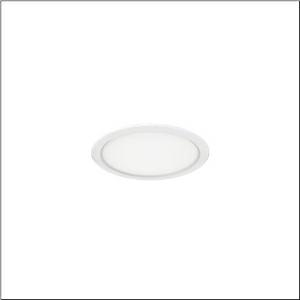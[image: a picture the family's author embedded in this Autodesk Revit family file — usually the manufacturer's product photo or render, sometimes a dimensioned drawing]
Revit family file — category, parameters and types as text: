
# Revit family: lunis_41_eco_51ds107d43b
name_source: partatom
category: Lighting Fixtures
units: mm (PartAtom-declared; Revit-internal decimal feet)

## family parameters
Cut with Voids When Loaded = No
Host = Face
Light Source = No
Part Type = Normal
Room Calculation Point = No
Round Connector Dimension = Use Diameter
Shared = No

## types (1)
- Lunis 41 Eco (1 x LED, 1580 lm, 12 W, 4000K)
    Apparent Load = 12 VA
    CIE Flux Codes = 47 80 97 100 100
    Color Rendering = 80
    Color Temperature = 4000K
    Default Elevation = 1800 mm
    Description = Lunis 41,  Eco, downlight, light emission: direct distribution, LED rated luminous flux: 1.580lm, light colour: 840, mains connection: 230V, AC, 50/60Hz, housing, round, of aluminium, coated, traffic white (RAL 9016), diameter: 166mm, recess depth: 54mm, protection rating (complete): IP20, protection rating (on room side): IP40, insulation class (complete): insulation class II (safety insulation), certification: CE, permissible ambient temperature for indoor applications: -20..+40°C, packaging unit: 1 piece
    Height = 0 mm  [stored 0 ft]
    Lamp = 1 x LED
    Lamp Light Flux = 1580 lm
    Lamp Power = 12 W
    Lamp count = 1
    Length = 166 mm
    Luminous efficacy = 132 lm/W
    Manufacturer = Siteco
    ModVariant = No
    Model = 51DS107D43B
    Mounting Place = Ceiling
    Mounting Type = Recessed
    Number of Poles = 1
    OnlyDefault = Yes
    Power Factor = 1
    Product Name = Lunis 41 Eco
    Product group = downlight
    ProductGroupID = 401
    Protection Class = Protection class II
    Protection Degree = IP 20
    RLX_Detail_Level = 1
    RLX_Emergency_Light_Flux = 0 lm
    RLX_Emergency_Type = 0
    RLX_Emergency_Type_DB = No
    RlxData = <blob elided: 8885 chars, md5=3a8b84c3>
    Socket = socket
    Standby Power = 0 W
    System Light Flux = 1580 lm
    System Power = 12 W
    Type Comments = Product without accessories
    Type Image = l_1345912.jpg
    URL = http://relux.com
    VarID = ---
    Voltage = 0 V
    Weight = 0.00 kg
    Width = 0 mm  [stored 0 ft]

note: [stored X ft] marks values corroborated as IEEE doubles in the binary element streams (Revit-internal decimal feet)

## geometry (parser evidence)
native form markers: Sweep x8
no freeform markers — native parametric forms only
